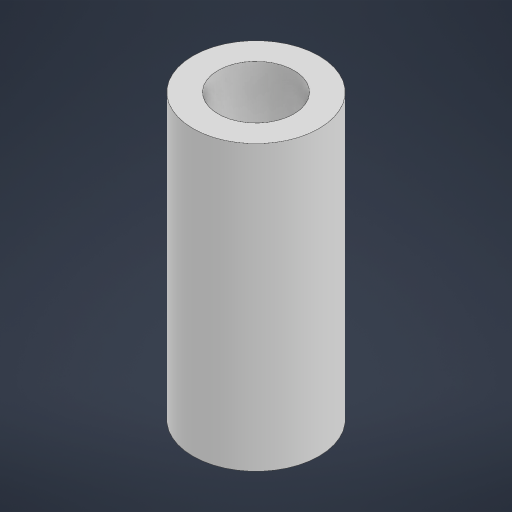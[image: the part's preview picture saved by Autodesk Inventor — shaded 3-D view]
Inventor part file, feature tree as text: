
AUTODESK INVENTOR PART (.ipt)
format: ipt  version: 2024.2 (Build 282272000, 272)  size: 158,208 bytes
history: native  units: mm
features: extrude x1, sketch x1
ambient origin geometry x8: Origin, YZ Plane, XZ Plane, XY Plane, X Axis, Y Axis, Z Axis, Center Point
bodies: Solid1 (feature_tree)
feature tree (2):
  extrude  "Extrusion1"  Depth=9.0mm
  sketch  "Sketch1"  dims[d0=2.4mm d1=4.0mm d2=9.0mm d3=0.0mm]
